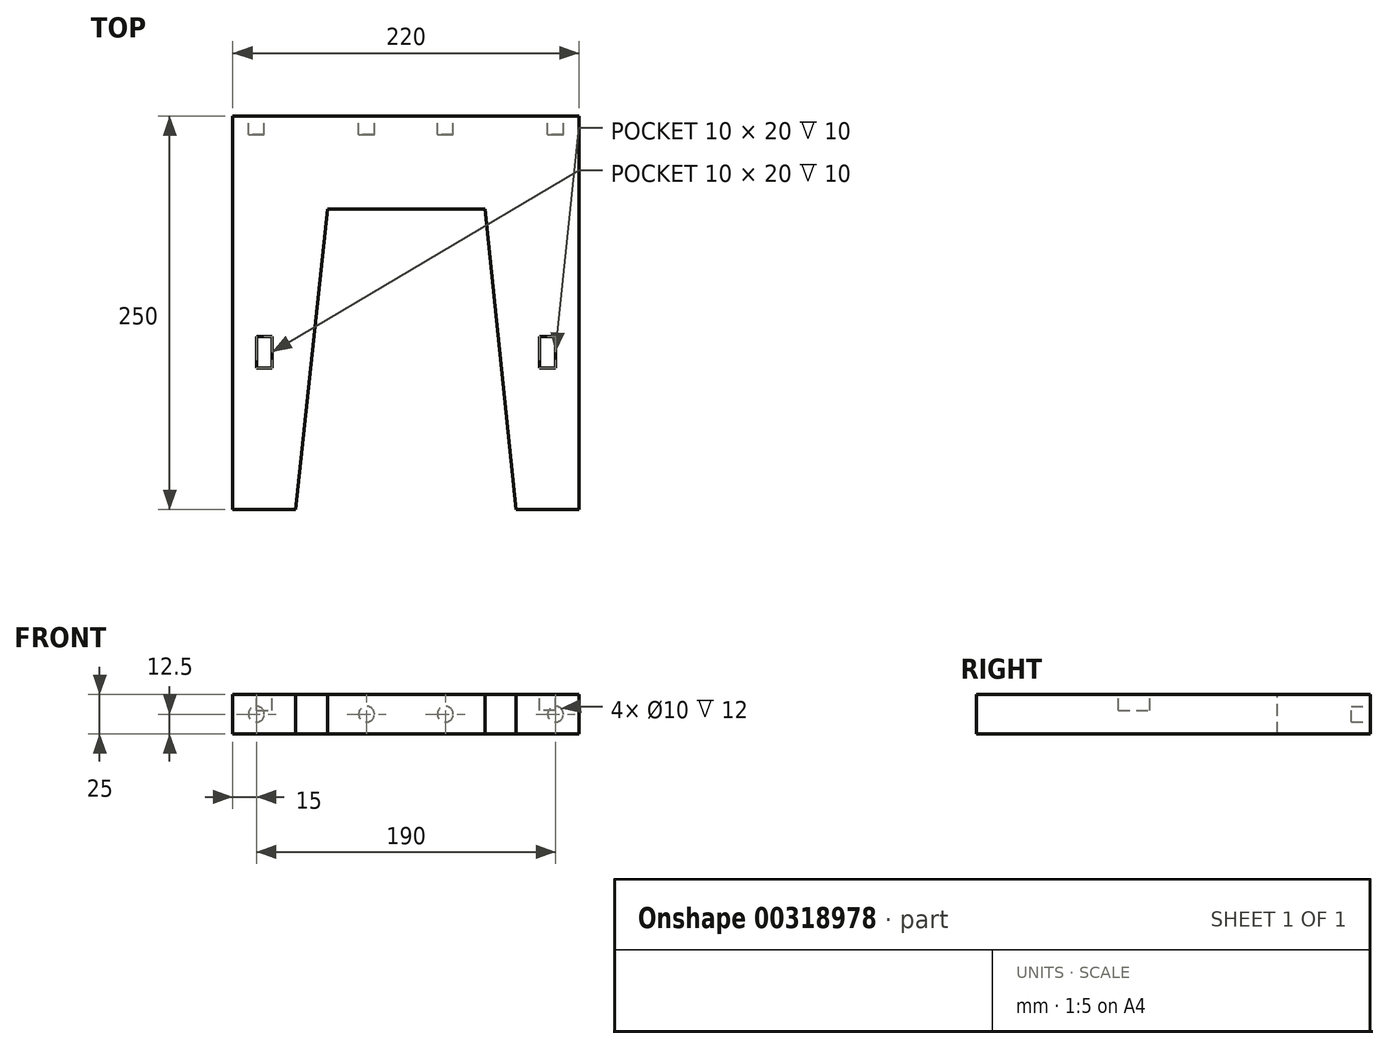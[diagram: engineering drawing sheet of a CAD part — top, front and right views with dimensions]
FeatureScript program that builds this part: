
annotation { "Feature Type Name" : "Feature", "Feature Type Description" : "" }
export const myFeature = defineFeature(function(context is Context, id is Id, definition is map)
    precondition{}
    {
        {
            var Q0;
            Q0=qCreatedBy(makeId("Top.planeOp"),FACE);
            var sketch = newSketch(context, id + "F0", { "sketchPlane" : qUnion([Q0])});
            skLineSegment(sketch, "E0.bottom", {"start": v(110, 125) * mm, "end": v(-110, 125) * mm});
            skLineSegment(sketch, "E0.left", {"start": v(110, 125) * mm, "end": v(110, -125) * mm});
            skLineSegment(sketch, "E0.right", {"start": v(-110, 125) * mm, "end": v(-110, -125) * mm});
            skPoint(sketch, "E0.middle", {"position": v(0, 0) * mm});
            skLineSegment(sketch, "E1", {"start": v(-110, -125) * mm, "end": v(-70, -125) * mm});
            skLineSegment(sketch, "E2", {"start": v(-70, -125) * mm, "end": v(-49.67, 66) * mm});
            skLineSegment(sketch, "E3", {"start": v(-49.67, 66) * mm, "end": v(50.33, 66) * mm});
            skLineSegment(sketch, "E4", {"start": v(50.33, 66) * mm, "end": v(70, -125) * mm});
            skLineSegment(sketch, "E5", {"start": v(70, -125) * mm, "end": v(110, -125) * mm});
            skPoint(sketch, "E6", {"position": v(0.33, 66) * mm});
            skSolve(sketch);
        }
        {
            var Q0;
            Q0=qSketchRegion(id+"F0",true);
            extrude(context, id + "F1", {"entities" : qUnion([Q0]), "depth" : 25 * mm});
        }
        {
            var Q0;
            Q0=makeQuery(id+"F1.opExtrude","SWEPT_FACE",FACE,{"disambiguationData":[OSD([sQuery(id+"F0.wireOp",EDGE,"E0.bottom")])]});
            var sketch = newSketch(context, id + "F2", { "sketchPlane" : qUnion([Q0])});
            skLineSegment(sketch, "E7", {"start": v(-110, 12.5) * mm, "end": v(110, 12.5) * mm, "construction": true});
            skPoint(sketch, "E8", {"position": v(-25, 12.5) * mm});
            skPoint(sketch, "E9", {"position": v(25, 12.5) * mm});
            skPoint(sketch, "E10", {"position": v(-95, 12.5) * mm});
            skPoint(sketch, "E11", {"position": v(95, 12.5) * mm});
            skCircle(sketch, "E12", {"center": v(95, 12.5) * mm, "radius": 5 * mm});
            skCircle(sketch, "E13", {"center": v(25, 12.5) * mm, "radius": 5 * mm});
            skCircle(sketch, "E14", {"center": v(-25, 12.5) * mm, "radius": 5 * mm});
            skCircle(sketch, "E15", {"center": v(-95, 12.5) * mm, "radius": 5 * mm});
            skSolve(sketch);
        }
        {
            var Q0;
            Q0=qSketchRegion(id+"F2",true);
            extrude(context, id + "F3", {"entities" : qUnion([Q0]), "operationType" : NewBodyOperationType.REMOVE, "oppositeDirection" : true, "depth" : 12 * mm});
        }
        {
            var Q0;
            Q0=makeQuery(id+"F1.opExtrude","CAP_FACE",FACE,{"disambiguationData":[OSD([sQuery(id+"F0.wireOp",EDGE,"E0.bottom"),sQuery(id+"F0.wireOp",EDGE,"E0.left"),sQuery(id+"F0.wireOp",EDGE,"E0.right"),sQuery(id+"F0.wireOp",EDGE,"E1"),sQuery(id+"F0.wireOp",EDGE,"E2"),sQuery(id+"F0.wireOp",EDGE,"E3"),sQuery(id+"F0.wireOp",EDGE,"E4"),sQuery(id+"F0.wireOp",EDGE,"E5")])],"isStart":true});
            var sketch = newSketch(context, id + "F4", { "sketchPlane" : qUnion([Q0])});
            skLineSegment(sketch, "E16", {"start": v(-95, 125) * mm, "end": v(-95, 35) * mm, "construction": true});
            skLineSegment(sketch, "E17", {"start": v(-95, 35) * mm, "end": v(-110, 35) * mm, "construction": true});
            skLineSegment(sketch, "E18.bottom", {"start": v(-95, 35) * mm, "end": v(-85, 35) * mm});
            skLineSegment(sketch, "E18.top", {"start": v(-95, 15) * mm, "end": v(-85, 15) * mm});
            skLineSegment(sketch, "E18.left", {"start": v(-95, 35) * mm, "end": v(-95, 15) * mm});
            skLineSegment(sketch, "E18.right", {"start": v(-85, 35) * mm, "end": v(-85, 15) * mm});
            skLineSegment(sketch, "E19", {"start": v(0, 0) * mm, "end": v(0, 76.5) * mm});
            skLineSegment(sketch, "E20.MirrorCS", {"start": v(95, 35) * mm, "end": v(85, 35) * mm});
            skLineSegment(sketch, "E21.MirrorCS", {"start": v(95, 15) * mm, "end": v(85, 15) * mm});
            skLineSegment(sketch, "E22.MirrorCS", {"start": v(95, 35) * mm, "end": v(110, 35) * mm, "construction": true});
            skLineSegment(sketch, "E23.MirrorCS", {"start": v(95, 35) * mm, "end": v(95, 15) * mm});
            skLineSegment(sketch, "E24.MirrorCS", {"start": v(85, 35) * mm, "end": v(85, 15) * mm});
            skSolve(sketch);
        }
        {
            var Q0;
            Q0=qSketchRegion(id+"F4",true);
            extrude(context, id + "F5", {"entities" : qUnion([Q0]), "operationType" : NewBodyOperationType.REMOVE, "oppositeDirection" : true, "depth" : 10 * mm});
        }
        {
            var Q0;
            Q0=qCreatedBy(makeId("Top.planeOp"),FACE);
            cPlane(context, id + "F6", {"entities" : qUnion([Q0]), "cplaneType" : CPlaneType.OFFSET, "offset" : 34 * mm, "oppositeDirection" : true, "width" : 150 * mm, "height" : 150 * mm});
        }
        {
            var Q0;
            Q0=makeQuery(id+"F1.opExtrude","SWEPT_BODY",BODY,{"disambiguationData":[OSD([sQuery(id+"F0.wireOp",EDGE,"E0.bottom"),sQuery(id+"F0.wireOp",EDGE,"E0.left"),sQuery(id+"F0.wireOp",EDGE,"E0.right"),sQuery(id+"F0.wireOp",EDGE,"E1"),sQuery(id+"F0.wireOp",EDGE,"E2"),sQuery(id+"F0.wireOp",EDGE,"E3"),sQuery(id+"F0.wireOp",EDGE,"E4"),sQuery(id+"F0.wireOp",EDGE,"E5")])]});
            var Q1;
            Q1=qCreatedBy(id+"F6.planeOp",FACE);
            mirror(context, id + "F7", {"entities" : qUnion([Q0]), "mirrorPlane" : qUnion([Q1])});
        }
        {
            var Q0;
            Q0=makeQuery(id+"F1.opExtrude","SWEPT_BODY",BODY,{"disambiguationData":[OSD([sQuery(id+"F0.wireOp",EDGE,"E0.bottom"),sQuery(id+"F0.wireOp",EDGE,"E0.left"),sQuery(id+"F0.wireOp",EDGE,"E0.right"),sQuery(id+"F0.wireOp",EDGE,"E1"),sQuery(id+"F0.wireOp",EDGE,"E2"),sQuery(id+"F0.wireOp",EDGE,"E3"),sQuery(id+"F0.wireOp",EDGE,"E4"),sQuery(id+"F0.wireOp",EDGE,"E5")])]});
            deleteBodies(context, id + "F8", {"entities" : qUnion([Q0])});
        }
    });
